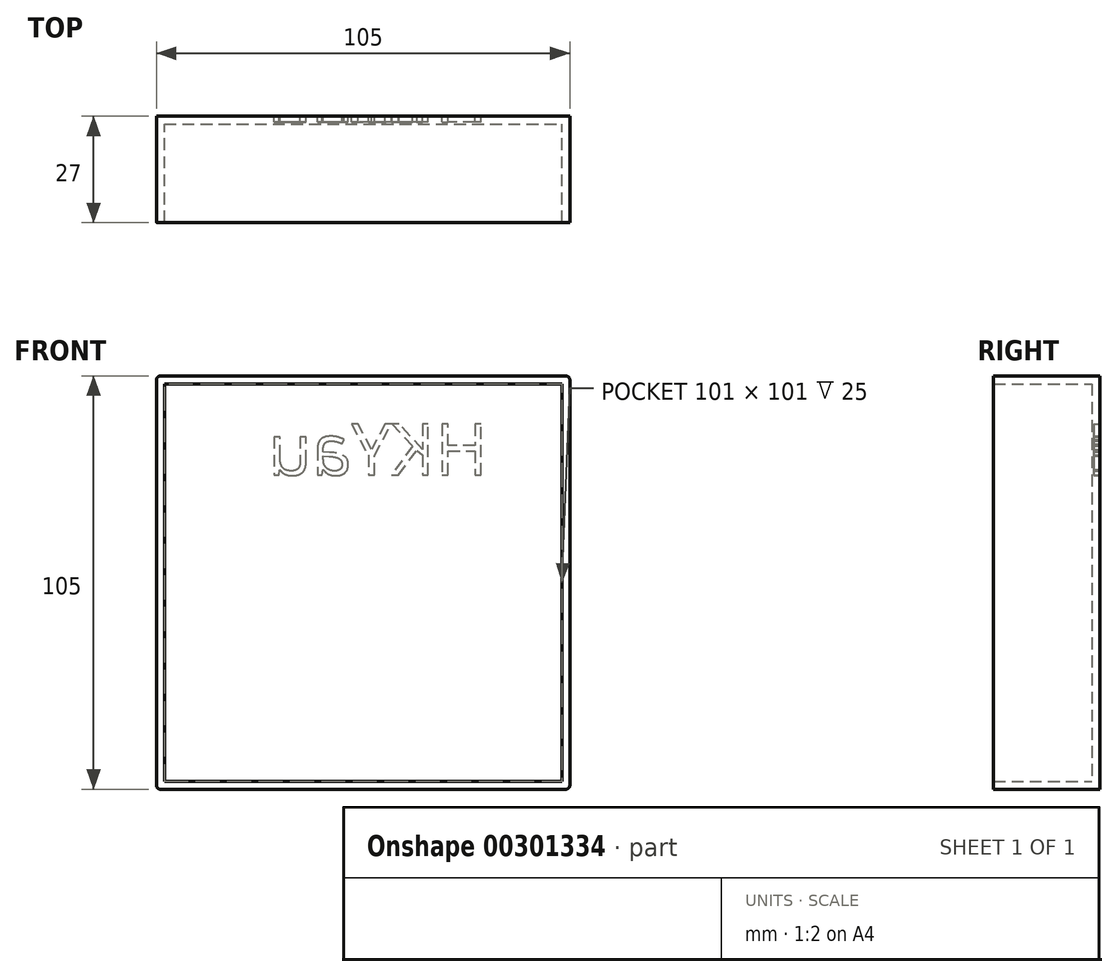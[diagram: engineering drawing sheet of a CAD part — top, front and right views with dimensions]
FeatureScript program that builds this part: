
annotation { "Feature Type Name" : "Feature", "Feature Type Description" : "" }
export const myFeature = defineFeature(function(context is Context, id is Id, definition is map)
    precondition{}
    {
        {
            var Q0;
            Q0=qCreatedBy(makeId("Front.planeOp"),FACE);
            var sketch = newSketch(context, id + "F0", { "sketchPlane" : qUnion([Q0])});
            skLineSegment(sketch, "E0.bottom", {"start": v(-37.92, 57.9) * mm, "end": v(67.08, 57.9) * mm});
            skLineSegment(sketch, "E0.top", {"start": v(-37.92, -47.1) * mm, "end": v(67.08, -47.1) * mm});
            skLineSegment(sketch, "E0.left", {"start": v(-37.92, 57.9) * mm, "end": v(-37.92, -47.1) * mm});
            skLineSegment(sketch, "E0.right", {"start": v(67.08, 57.9) * mm, "end": v(67.08, -47.1) * mm});
            skSolve(sketch);
        }
        {
            var Q0;
            Q0=makeQuery(id+"F0.imprint","IMPRINT",FACE,{"disambiguationData":[TD([[makeQuery(id+"F0.imprint","IMPRINT",EDGE,{"derivedFrom":sQuery(id+"F0.wireOp",EDGE,"E0.bottom")}),-1.0]])]});
            extrude(context, id + "F1", {"entities" : qUnion([Q0]), "depth" : 27 * mm});
        }
        {
            var Q0;
            Q0=makeQuery(id+"F1.opExtrude","CAP_FACE",FACE,{"disambiguationData":[OSD([sQuery(id+"F0.wireOp",EDGE,"E0.bottom"),sQuery(id+"F0.wireOp",EDGE,"E0.top"),sQuery(id+"F0.wireOp",EDGE,"E0.left"),sQuery(id+"F0.wireOp",EDGE,"E0.right")])],"isStart":false});
            shell(context, id + "F2", {"entities" : qUnion([Q0]), "thickness" : 2 * mm});
        }
        {
            var Q0;
            Q0=makeQuery(id+"F1.opExtrude","CAP_FACE",FACE,{"disambiguationData":[OSD([sQuery(id+"F0.wireOp",EDGE,"E0.bottom"),sQuery(id+"F0.wireOp",EDGE,"E0.top"),sQuery(id+"F0.wireOp",EDGE,"E0.left"),sQuery(id+"F0.wireOp",EDGE,"E0.right")])],"isStart":true});
            var sketch = newSketch(context, id + "F3", { "sketchPlane" : qUnion([Q0])});
            skText(sketch, "E1", { "text": "HKYau", "fontName": "OpenSans-Regular.ttf"});
            const initialGuessF3  = {"E1": [-0.04629, 0.03276, 1, 0, 0.01306]};
            skSetInitialGuess(sketch, initialGuessF3);
            skSolve(sketch);
        }
        {
            var Q0;
            Q0 = qSketchRegion(id + "F3", true);
            extrude(context, id + "F4", {"entities" : qUnion([Q0]), "operationType" : NewBodyOperationType.REMOVE, "oppositeDirection" : true, "depth" : 1.5 * mm});
        }
        {
            var Q0;
            Q0=makeQuery(id+"F1.opExtrude","SWEPT_EDGE",EDGE,{"disambiguationData":[OSD([sQuery(id+"F0.wireOp",EDGE,"E0.top"),sQuery(id+"F0.wireOp",EDGE,"E0.right")])]});
            var Q1;
            Q1=makeQuery(id+"F1.opExtrude","SWEPT_EDGE",EDGE,{"disambiguationData":[OSD([sQuery(id+"F0.wireOp",EDGE,"E0.top"),sQuery(id+"F0.wireOp",EDGE,"E0.left")])]});
            var Q2;
            Q2=makeQuery(id+"F1.opExtrude","SWEPT_EDGE",EDGE,{"disambiguationData":[OSD([sQuery(id+"F0.wireOp",EDGE,"E0.bottom"),sQuery(id+"F0.wireOp",EDGE,"E0.right")])]});
            var Q3;
            Q3=makeQuery(id+"F1.opExtrude","SWEPT_EDGE",EDGE,{"disambiguationData":[OSD([sQuery(id+"F0.wireOp",EDGE,"E0.bottom"),sQuery(id+"F0.wireOp",EDGE,"E0.left")])]});
            fillet(context, id + "F5", {"entities" : qUnion([Q0, Q1, Q2, Q3]), "radius" : 1 * mm, "tangentPropagation" : true, "allowEdgeOverflow" : false});
        }
    });
